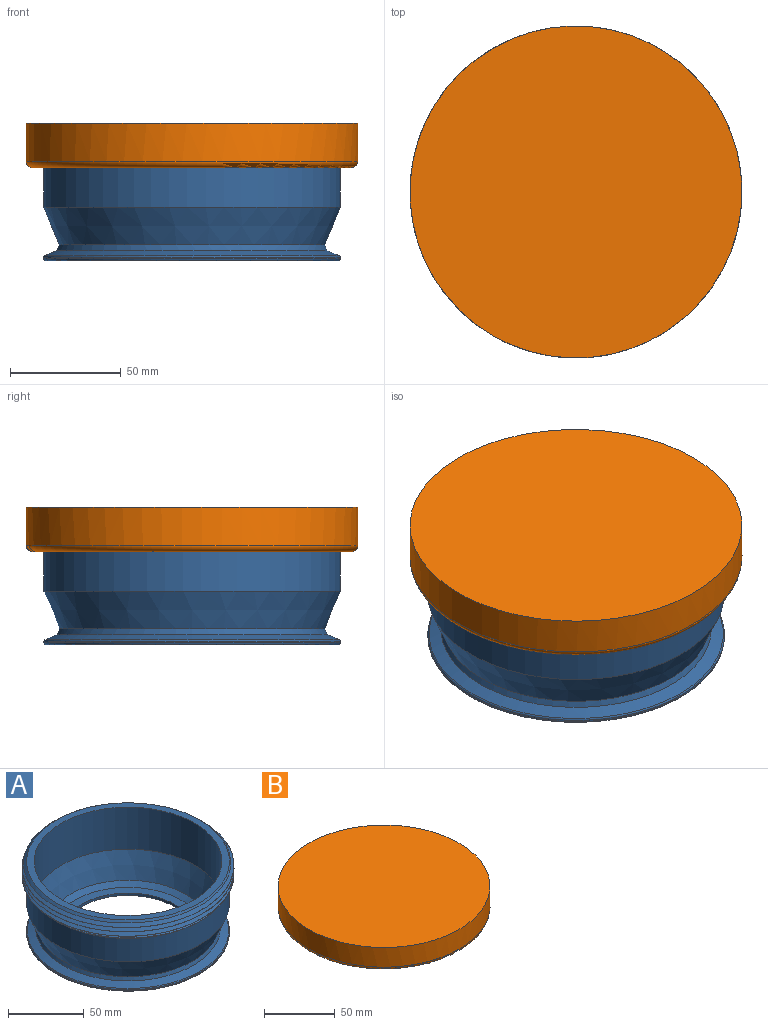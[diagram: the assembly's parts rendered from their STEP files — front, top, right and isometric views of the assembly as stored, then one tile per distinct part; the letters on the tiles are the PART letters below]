
ASSEMBLY  parts=2 mates=1
PART A: 19 faces, bbox 145x161.7x59.9 mm
  f0: plane 134x134mm, normal (0,0,1), area 2026.3mm2, adj f7,f13
  f1: cylinder r=70mm len=140mm, axis (0,0,1), area 39.9mm2, adj f12,f13,f14,f15
  f2: cylinder r=67mm len=134mm, axis (0,0,1), area 7971.1mm2, adj f3,f12
  f3: cone r=59.18mm half-angle=22.6deg, axis (0,0,1), area 7328.7mm2, adj f2,f16
  f4: cone r=67mm half-angle=67.4deg, axis (0,0,-1), area 2377.2mm2, adj f16,f17
  f5: cylinder r=67mm len=134mm, axis (0,0,1), area 280.4mm2, adj f17,f18
  f6: plane 132.4x132.4mm, normal (0,0,-1), area 7959mm2, adj f11,f18
  f7: cylinder r=62mm len=124mm, axis (0,0,-1), area 13219.8mm2, adj f0,f8
  f8: cone r=62mm half-angle=23.3deg, axis (0,0,1), area 7640.5mm2, adj f7,f9
  f9: cone r=53.69mm half-angle=56.6deg, axis (0,0,1), area 1624.7mm2, adj f8,f10
  f10: plane 99x99mm, normal (0,0,1), area 1888.9mm2, adj f9,f11
  f11: cylinder r=43mm len=86mm, axis (0,0,-1), area 540.4mm2, adj f6,f10
  f12: cone r=70mm half-angle=45deg, axis (0,0,1), area 916.3mm2, adj f1,f2,f14,f15
  f13: cone r=67mm half-angle=45deg, axis (0,0,-1), area 917.7mm2, adj f0,f1,f14,f15
  f14: bspline ~161.66x140mm, area 5100.4mm2, adj f1,f12,f13,f15
  f15: bspline ~161.66x140mm, area 5101.7mm2, adj f1,f12,f13,f14
  f16: cone r=59.95mm half-angle=22.4deg, axis (0,0,-1), area 1075mm2, adj f3,f4
  f17: torus R=66.2mm, axis (0,0,-1), area 395.4mm2, adj f4,f5
  f18: torus R=66.2mm, axis (0,0,1), area 526.7mm2, adj f5,f6
PART B: 19 faces, bbox 162.4x164.5x20.3 mm
  f0: plane 143x143mm, normal (0,0,1), area 128.9mm2, adj f8,f9,f10,f11,f13
  f1: plane 143x143mm, normal (0,0,-1), area 16041.9mm2, adj f9,f10,f11,f13,f15
  f2: plane 150x150mm, normal (0,0,1), area 17671.5mm2, adj f3
  f3: cylinder r=75mm len=150mm, axis (0,0,1), area 8011.1mm2, adj f2,f18
  f4: plane 144x144mm, normal (0,0,-1), area 449.2mm2, adj f5,f18
  f5: cylinder r=71mm len=142mm, axis (0,0,1), area 781mm2, adj f4,f6,f12,f14,f16
  f6: cylinder r=71mm len=142mm, axis (0,0,1), area 119.5mm2, adj f5,f7,f14,f15,f17
  f7: cylinder r=71mm len=142mm, axis (0,0,1), area 118.8mm2, adj f6,f8,f14,f15
  f8: cylinder r=71mm len=142mm, axis (0,0,1), area 92.6mm2, adj f0,f7,f14,f15
  f9: cylinder r=71.5mm len=143mm, axis (0,0,1), area 1316.8mm2, adj f0,f1
  f10: bspline ~164.5x142.46mm, area 85.9mm2, adj f0,f1,f11,f15
  f11: cylinder r=71.23mm len=142.46mm, axis (0,0,1), area 664.2mm2, adj f0,f1,f10,f13
  f12: plane 0.47x0.41mm, normal (0,-1,0), area 0.1mm2, adj f5,f16,f17
  f13: plane 3.02x2.94mm, normal (0.99,-0.1,0), area 5.1mm2, adj f0,f1,f11,f14,f15
  f14: bspline ~163.97x142mm, area 5279.2mm2, adj f5,f6,f7,f8,f13,f15,f16
  f15: bspline ~163.97x142mm, area 5264.2mm2, adj f1,f6,f7,f8,f10,f13,f14,f16
  f16: bspline ~4.68x3.39mm, area 4.2mm2, adj f5,f12,f14,f15,f17
  f17: bspline ~4.68x3.39mm, area 4mm2, adj f6,f12,f15,f16
  f18: torus R=72mm, axis (0,0,-1), area 2188.4mm2, adj f3,f4
PLACE A t=(-39.72,-6.6,-6.78)mm fixed
PLACE B rot(axis=(0,0,-1),169.5deg) t=(-39.7,-6.52,76.59)mm
MATE revolute B.f1 <-> A.f1  axis (0,0,-1) through (-39.72,-6.6,51.22)mm
